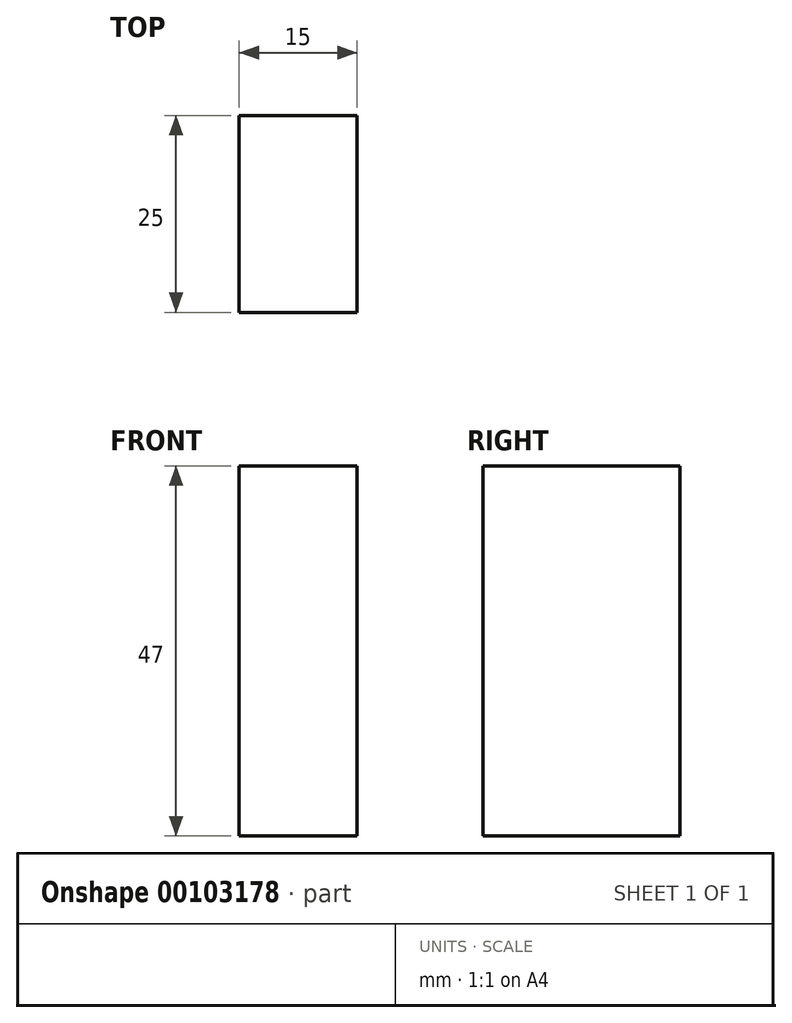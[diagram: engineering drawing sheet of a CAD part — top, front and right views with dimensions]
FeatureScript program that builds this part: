
annotation { "Feature Type Name" : "Feature", "Feature Type Description" : "" }
export const myFeature = defineFeature(function(context is Context, id is Id, definition is map)
    precondition{}
    {
        {
            var Q0;
            Q0=qCreatedBy(makeId("Front.planeOp"),FACE);
            var sketch = newSketch(context, id + "F0", { "sketchPlane" : qUnion([Q0])});
            skLineSegment(sketch, "E0.bottom", {"start": v(7.5, -23.5) * mm, "end": v(-7.5, -23.5) * mm});
            skLineSegment(sketch, "E0.top", {"start": v(7.5, 23.5) * mm, "end": v(-7.5, 23.5) * mm});
            skLineSegment(sketch, "E0.left", {"start": v(7.5, -23.5) * mm, "end": v(7.5, 23.5) * mm});
            skLineSegment(sketch, "E0.right", {"start": v(-7.5, -23.5) * mm, "end": v(-7.5, 23.5) * mm});
            skPoint(sketch, "E0.middle", {"position": v(0, 0) * mm});
            skSolve(sketch);
        }
        {
            var Q0;
            Q0=makeQuery(id+"F0.imprint","IMPRINT",FACE,{"disambiguationData":[TD([[makeQuery(id+"F0.imprint","IMPRINT",EDGE,{"derivedFrom":sQuery(id+"F0.wireOp",EDGE,"E0.bottom")}),-1.0]])]});
            extrude(context, id + "F1", {"entities" : qUnion([Q0]), "depth" : 25 * mm});
        }
    });
